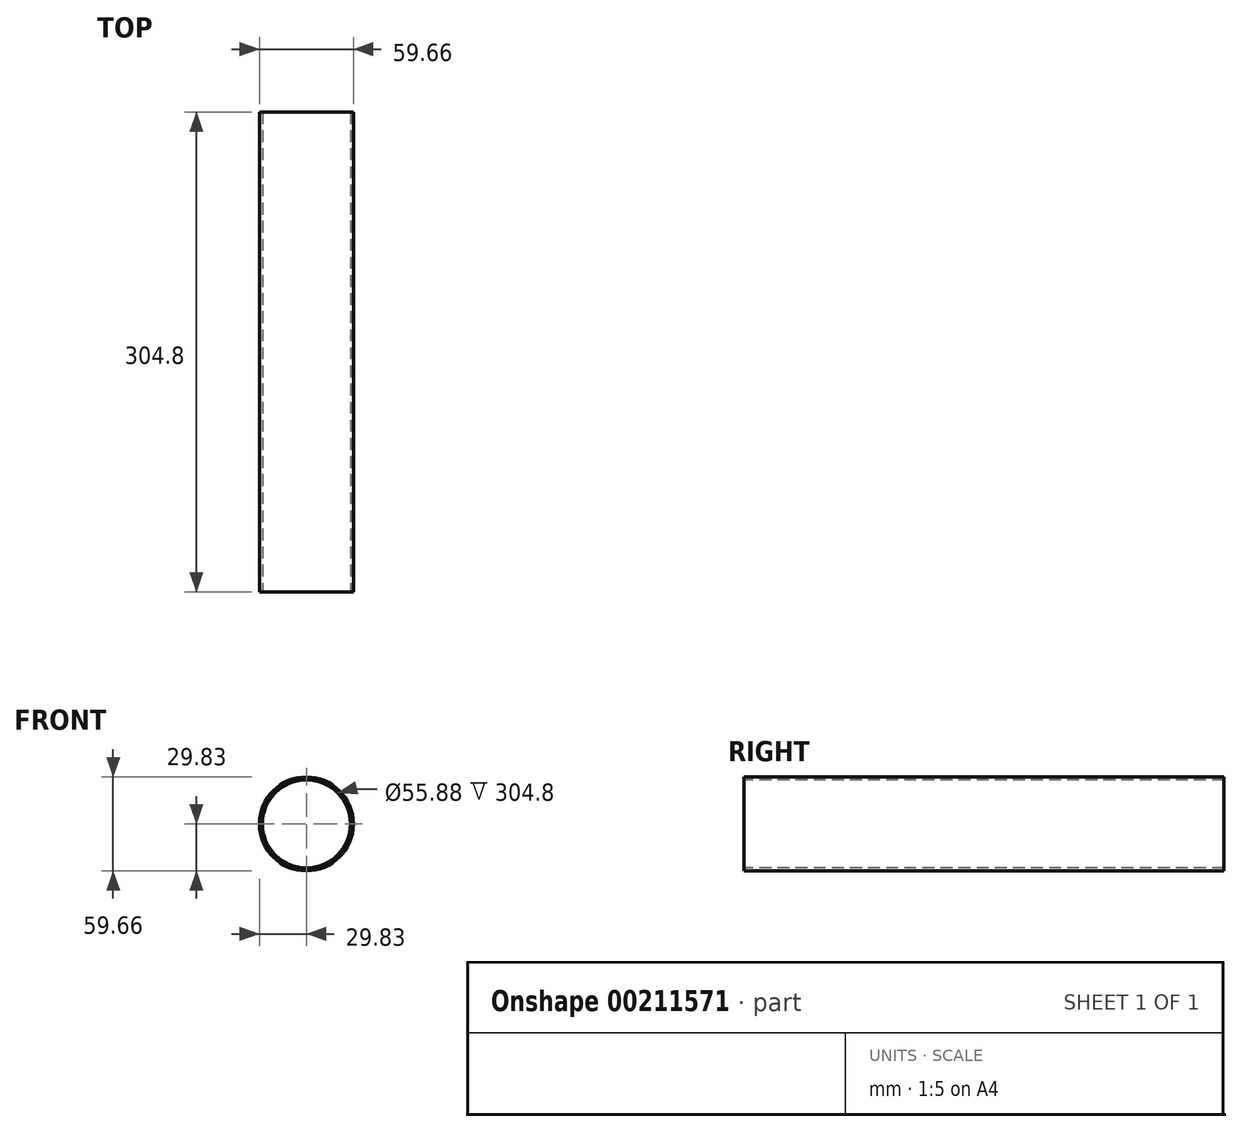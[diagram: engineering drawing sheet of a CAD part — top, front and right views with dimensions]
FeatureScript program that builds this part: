
annotation { "Feature Type Name" : "Feature", "Feature Type Description" : "" }
export const myFeature = defineFeature(function(context is Context, id is Id, definition is map)
    precondition{}
    {
        {
            var Q0;
            Q0=qCreatedBy(makeId("Front.planeOp"),FACE);
            var sketch = newSketch(context, id + "F0", { "sketchPlane" : qUnion([Q0])});
            skCircle(sketch, "E0", {"center": v(0, 0) * mm, "radius": 29.83 * mm});
            skSolve(sketch);
        }
        {
            var Q0;
            Q0=makeQuery(id+"F0.imprint","IMPRINT",FACE,{"disambiguationData":[TD([[makeQuery(id+"F0.imprint","IMPRINT",EDGE,{"derivedFrom":sQuery(id+"F0.wireOp",EDGE,"E0")}),1.0]])]});
            extrude(context, id + "F1", {"entities" : qUnion([Q0]), "oppositeDirection" : true, "depth" : 304.8 * mm});
        }
        {
            var Q0;
            Q0=qCreatedBy(makeId("Front.planeOp"),FACE);
            var sketch = newSketch(context, id + "F2", { "sketchPlane" : qUnion([Q0])});
            skCircle(sketch, "E1", {"center": v(0, 0) * mm, "radius": 27.94 * mm});
            skSolve(sketch);
        }
        {
            var Q0;
            Q0=qSketchRegion(id+"F2",true);
            var Q1;
            Q1=makeQuery(id+"F2.imprint","IMPRINT",FACE,{"disambiguationData":[TD([[makeQuery(id+"F2.imprint","IMPRINT",EDGE,{"derivedFrom":sQuery(id+"F2.wireOp",EDGE,"E1")}),1.0]])]});
            extrude(context, id + "F3", {"entities" : qUnion([Q0, Q1]), "operationType" : NewBodyOperationType.REMOVE, "oppositeDirection" : true, "depth" : 304.8 * mm});
        }
    });
